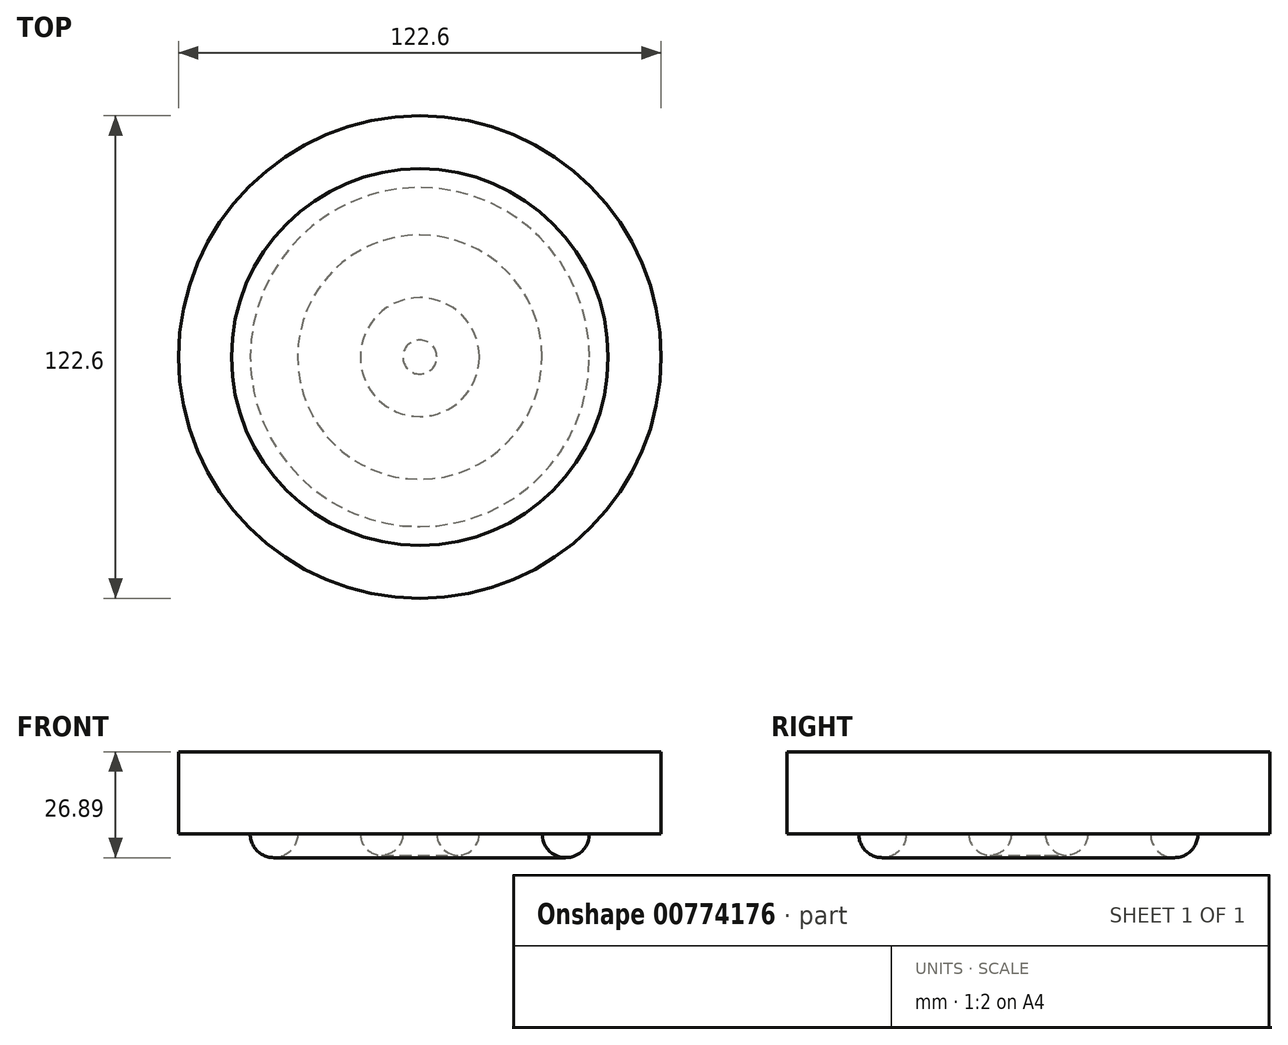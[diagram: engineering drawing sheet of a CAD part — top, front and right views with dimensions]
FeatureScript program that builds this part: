
annotation { "Feature Type Name" : "Feature", "Feature Type Description" : "" }
export const myFeature = defineFeature(function(context is Context, id is Id, definition is map)
    precondition{}
    {
        {
            var Q0;
            Q0=qCreatedBy(makeId("Front.planeOp"),FACE);
            var sketch = newSketch(context, id + "F0", { "sketchPlane" : qUnion([Q0])});
            skLineSegment(sketch, "E0.bottom", {"start": v(0, 20.87) * mm, "end": v(47.86, 20.87) * mm});
            skLineSegment(sketch, "E0.top", {"start": v(0, 0) * mm, "end": v(47.86, 0) * mm});
            skLineSegment(sketch, "E0.left", {"start": v(0, 20.87) * mm, "end": v(0, 0) * mm});
            skLineSegment(sketch, "E0.right", {"start": v(47.86, 20.87) * mm, "end": v(47.86, 0) * mm});
            skLineSegment(sketch, "E1.bottom", {"start": v(47.86, 0) * mm, "end": v(61.3, 0) * mm});
            skLineSegment(sketch, "E1.top", {"start": v(47.86, 20.85) * mm, "end": v(61.3, 20.85) * mm});
            skLineSegment(sketch, "E1.left", {"start": v(47.86, 0) * mm, "end": v(47.86, 20.85) * mm});
            skLineSegment(sketch, "E1.right", {"start": v(61.3, 0) * mm, "end": v(61.3, 20.85) * mm});
            skCircle(sketch, "E2", {"center": v(9.72, 0) * mm, "radius": 5.4 * mm});
            skCircle(sketch, "E3", {"center": v(37.07, 0) * mm, "radius": 6.02 * mm});
            skSolve(sketch);
        }
        {
            var Q0;
            {var subQ0=sQuery(id+"F0.wireOp",EDGE,"E3");var subQ1=sQuery(id+"F0.wireOp",EDGE,"E0.top");var subQ2=makeQuery(id+"F0.imprint","INTERSECT",VERTEX,{"disambiguationData":[OD(0.0)],"derivedFrom":[subQ1,subQ0]});Q0=makeQuery(id+"F0.imprint","IMPRINT",FACE,{"disambiguationData":[TD([[makeQuery(id+"F0.imprint","IMPRINT",EDGE,{"disambiguationData":[TD([[subQ2,-1.0]])],"derivedFrom":subQ1}),-1.0]])]});}
            var Q1;
            {var subQ2=sQuery(id+"F0.wireOp",EDGE,"E1.bottom");Q1=makeQuery(id+"F0.imprint","IMPRINT",FACE,{"disambiguationData":[TD([[makeQuery(id+"F0.imprint","IMPRINT",EDGE,{"derivedFrom":subQ2}),1.0]])]});}
            var Q2;
            {var subQ0=sQuery(id+"F0.wireOp",EDGE,"E3");var subQ1=sQuery(id+"F0.wireOp",EDGE,"E0.top");var subQ2=makeQuery(id+"F0.imprint","INTERSECT",VERTEX,{"disambiguationData":[OD(0.0)],"derivedFrom":[subQ1,subQ0]});Q2=makeQuery(id+"F0.imprint","IMPRINT",FACE,{"disambiguationData":[TD([[makeQuery(id+"F0.imprint","IMPRINT",EDGE,{"disambiguationData":[TD([[subQ2,-1.0]])],"derivedFrom":subQ1}),1.0]])]});}
            var Q3;
            {var subQ10=sQuery(id+"F0.wireOp",EDGE,"E0.bottom");Q3=makeQuery(id+"F0.imprint","IMPRINT",FACE,{"disambiguationData":[TD([[makeQuery(id+"F0.imprint","IMPRINT",EDGE,{"derivedFrom":subQ10}),-1.0]])]});}
            var Q4;
            {var subQ0=sQuery(id+"F0.wireOp",EDGE,"E2");var subQ1=sQuery(id+"F0.wireOp",EDGE,"E0.top");var subQ2=makeQuery(id+"F0.imprint","INTERSECT",VERTEX,{"disambiguationData":[OD(0.0)],"derivedFrom":[subQ1,subQ0]});Q4=makeQuery(id+"F0.imprint","IMPRINT",FACE,{"disambiguationData":[TD([[makeQuery(id+"F0.imprint","IMPRINT",EDGE,{"disambiguationData":[TD([[subQ2,1.0]])],"derivedFrom":subQ1}),1.0]])]});}
            var Q5;
            {var subQ0=sQuery(id+"F0.wireOp",EDGE,"E2");var subQ1=sQuery(id+"F0.wireOp",EDGE,"E0.top");var subQ2=makeQuery(id+"F0.imprint","INTERSECT",VERTEX,{"disambiguationData":[OD(0.0)],"derivedFrom":[subQ1,subQ0]});Q5=makeQuery(id+"F0.imprint","IMPRINT",FACE,{"disambiguationData":[TD([[makeQuery(id+"F0.imprint","IMPRINT",EDGE,{"disambiguationData":[TD([[subQ2,1.0]])],"derivedFrom":subQ1}),-1.0]])]});}
            var Q6;
            Q6=sQuery(id+"F0.wireOp",EDGE,"E0.left");
            revolve(context, id + "F1", {"surfaceOperationType" : NewSurfaceOperationType.NEW, "entities" : qUnion([Q0, Q1, Q2, Q3, Q4, Q5]), "axis" : qUnion([Q6]), "revolveType" : RevolveType.FULL});
        }
    });
